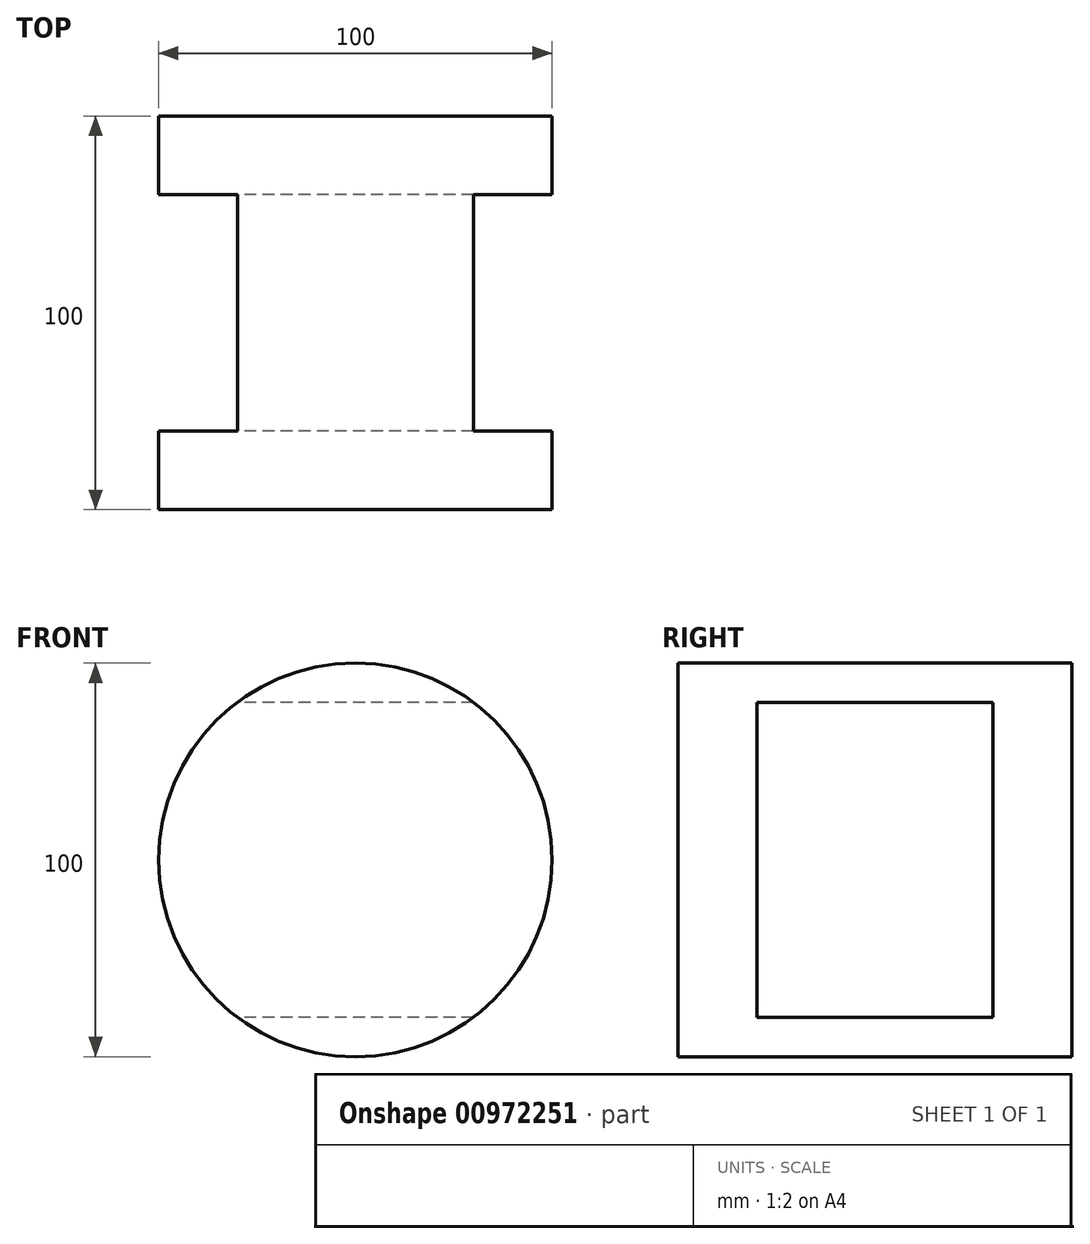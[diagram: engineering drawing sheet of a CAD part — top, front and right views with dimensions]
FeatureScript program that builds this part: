
annotation { "Feature Type Name" : "Feature", "Feature Type Description" : "" }
export const myFeature = defineFeature(function(context is Context, id is Id, definition is map)
    precondition{}
    {
        {
            var Q0;
            Q0=qCreatedBy(makeId("Front.planeOp"),FACE);
            var sketch = newSketch(context, id + "F0", { "sketchPlane" : qUnion([Q0])});
            skCircle(sketch, "E0", {"center": v(0, 0) * mm, "radius": 50 * mm});
            skSolve(sketch);
        }
        {
            var Q0;
            Q0=makeQuery(id+"F0.imprint","IMPRINT",FACE,{"disambiguationData":[TD([[makeQuery(id+"F0.imprint","IMPRINT",EDGE,{"derivedFrom":sQuery(id+"F0.wireOp",EDGE,"E0")}),1.0]])]});
            extrude(context, id + "F1", {"entities" : qUnion([Q0]), "endBound" : BoundingType.SYMMETRIC, "depth" : 100 * mm, "offsetDistance" : 25 * mm});
        }
        {
            var Q0;
            Q0=qCreatedBy(makeId("Right.planeOp"),FACE);
            var sketch = newSketch(context, id + "F2", { "sketchPlane" : qUnion([Q0])});
            skLineSegment(sketch, "E1.bottom", {"start": v(-30, 40) * mm, "end": v(30, 40) * mm});
            skLineSegment(sketch, "E1.top", {"start": v(-30, -40) * mm, "end": v(30, -40) * mm});
            skLineSegment(sketch, "E1.left", {"start": v(-30, 40) * mm, "end": v(-30, -40) * mm});
            skLineSegment(sketch, "E1.right", {"start": v(30, 40) * mm, "end": v(30, -40) * mm});
            skSolve(sketch);
        }
        {
            var Q0;
            Q0 = qSketchRegion(id + "F2", true);
            extrude(context, id + "F3", {"entities" : qUnion([Q0]), "operationType" : NewBodyOperationType.REMOVE, "endBound" : BoundingType.SYMMETRIC, "depth" : 200 * mm, "offsetDistance" : 25 * mm});
        }
    });
